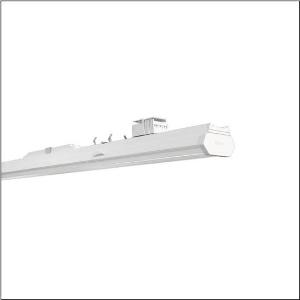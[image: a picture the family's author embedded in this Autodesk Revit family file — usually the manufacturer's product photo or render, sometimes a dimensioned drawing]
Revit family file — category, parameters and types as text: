
# Revit family: licross_11_protected_mo_51td117n485g
name_source: partatom
category: Lighting Fixtures
units: mm (PartAtom-declared; Revit-internal decimal feet)

## family parameters
Cut with Voids When Loaded = No
Host = Face
Light Source = No
Part Type = Normal
Room Calculation Point = No
Round Connector Dimension = Use Diameter
Shared = No

## types (1)
- Licross 11 Protected MO (1 x LED, 8680 lm, 48.6 W, 4000K)
    Apparent Load = 49 VA
    CIE Flux Codes = 83 94 98 100 100
    Color Rendering = 80
    Color Temperature = 4000K
    Default Elevation = 1800 mm
    Description = Licross 11 Protected MO, luminaire insert, of sheet steel, galvanised, coil coated, white, length: 1.500mm, width: 90mm, height: 101mm, LED rated luminous flux: 8.680lm, light colour: 840, SDCM (Standard Deviation of Colour Matching)MacAdam ≤ 2 SDCM (initial), control gear: ON/OFF, with plug, 3-pole, with phase selection, mains connection: 220..240V, AC, 50/60Hz, rated input power: 49W, internal wiring halogen-free, primary light control with lens, of plastic, primary optical cover: cover, of PMMA, light emission: direct distribution, primary light characteristic: symmetric, protection rating (complete): IP54, insulation class (complete): insulation class I (protective earthing), certification: CE, ENEC, VDE, UKCA, protection symbol: D if used in an environment with non-conductive dust loads with corresponding accessories, impact resistance: IK06, permissible ambient temperature for indoor applications: -25..+35°C, corresponds to IFS (International Featured Standards) requirements for safety and quality in the food industry, reducing of maximum allowable ambient temperature of 5°C with ceiling mounting, LABS conformity tested according to VDMA 24364:2018-05, The light source and the operating device comply with the requirements of the Ecodesign Regulation (EU) 2019/2020 and are replaceable in accordance with this regulation, packaging unit: 1 piece
    Height = 92 mm
    Lamp = 1 x LED
    Lamp Light Flux = 8680 lm
    Lamp Power = 48.6 W
    Lamp count = 1
    Length = 1500 mm
    Luminous efficacy = 179 lm/W
    Manufacturer = Siteco
    ModVariant = No
    Model = 51TD117N485G
    Mounting Place = Ceiling
    Mounting Type = Pendant
    Number of Poles = 1
    OnlyDefault = Yes
    Power Factor = 1
    Product Name = Licross 11 Protected MO
    Product group = luminaire insert | ceiling pendant
    ProductGroupID = 901
    Protection Class = Protection class I
    Protection Degree = IP 54
    RLX_Detail_Level = 1
    RLX_Emergency_Light_Flux = 0 lm
    RLX_Emergency_Type = 0
    RLX_Emergency_Type_DB = No
    RlxData = <blob elided: 20729 chars, md5=5d0e1a74>
    Socket = socket
    Standby Power = 0 W
    System Light Flux = 8680 lm
    System Power = 49 W
    Type Comments = Product without accessories
    Type Image = l_1256145.jpg
    URL = http://relux.com
    VarID = ---
    Voltage = 0 V
    Weight = 0.00 kg
    Width = 88 mm

## geometry (parser evidence)
native form markers: Blend x4, Sweep x11
no freeform markers — native parametric forms only
